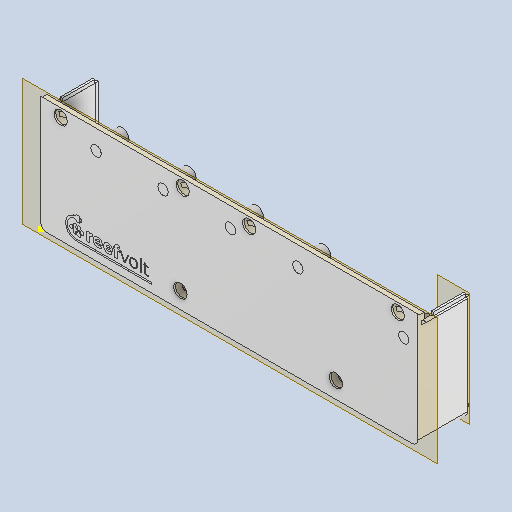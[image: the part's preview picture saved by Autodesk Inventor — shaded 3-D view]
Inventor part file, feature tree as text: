
AUTODESK INVENTOR PART (.ipt)
format: ipt  version: 2024.2 (Build 282272000, 272)  size: 966,656 bytes
history: native  units: in
note: dims shown in document units (in); Inventor stores cm internally (conversion verified against a paired STEP export)
features: reference x38, extrude x13, other x13, sketch x4, plane x3, chamfer x2, hole x1
ambient origin geometry x8: Origin, YZ Plane, XZ Plane, XY Plane, X Axis, Y Axis, Z Axis, Center Point
bodies: Solid1 (feature_tree)
feature tree (74):
  plane  "Work Plane1"
  plane  "Work Plane2"
  extrude  "Extrusion1"  Depth=0.1969in TaperAngle=0.0deg
  extrude  "Extrusion2"  Depth=0.0039in
  other  "Offset Top Of Cable Gland"
  other  "Offset from case bottom"
  extrude  "CableWall"  Depth=1.0in TaperAngle=0.0deg
  extrude  "CableInnerLid"  Depth=0.3937in TaperAngle=0.0deg
  extrude  "CableCutouts"  Depth=0.3937in
  extrude  "SideWallsToBottom"  Depth=0.3937in TaperAngle=0.0deg
  hole  "Hole1"  [1 undecoded]
  chamfer  "Chamfer1"  Distance=0.1575in
  extrude  "Extrusion8"  Depth=0.3937in
  extrude  "Extrusion9"  Depth=0.3937in
  plane  "Work Plane6"
  extrude  "LED Cutback"  Depth=0.3937in TaperAngle=0.0deg
  extrude  "LED Surface Boss"  Depth=0.3937in
  extrude  "Logo"  Depth=0.3937in
  extrude  "LED Tubes"  Depth=0.3937in TaperAngle=45.0deg
  extrude  "Extrusion14"  Depth=0.3937in
  chamfer  "Chamfer2"  Distance=0.0039in
  reference  "Reference2"
  sketch  "Sketch3"  dims[d0=0.125in d1=0.1969in d2=0.0in]
  reference  "Reference3"
  reference  "Reference4"
  reference  "Reference5"
  reference  "Reference6"
  reference  "Reference7"
  reference  "Reference8"
  reference  "Reference9"
  reference  "Reference10"
  reference  "Reference11"
  reference  "Reference12"
  reference  "Reference14"
  reference  "Reference15"
  sketch  "Sketch6"  dims[d3=0.0008in d4=0.0039in]
  reference  "Reference16"
  reference  "Reference17"
  reference  "Reference18"
  reference  "Reference19"
  reference  "Reference20"
  reference  "Reference23"
  reference  "Reference24"
  reference  "Reference25"
  reference  "Reference26"
  reference  "Reference27"
  reference  "Reference28"
  reference  "Reference29"
  reference  "Reference30"
  reference  "Reference31"
  reference  "Reference33"
  sketch  "Sketch13"  dims[d5=0.0039in d6=1.0in d7=0.0in]
  reference  "Reference34"
  reference  "Reference35"
  reference  "Reference36"
  reference  "Reference37"
  reference  "Reference38"
  sketch  "Sketch18"  dims[d8=0.1181in d9=1.0in d10=0.0in d11=0.1142in d12=0.0787in d13=0.0in d14=0.3937in d15=0.0in d16=0.1575in d17=0.0039in d18=0.0039in d21=0.3937in d22=0.0in d23=0.0039in d24=0.0079in d29=0.129in d30=0.75in d31=0.3in d32=0.1181in d33=0.5635in d34=1.0in d35=0.8108in d36=0.08in d37=0.125in d38=45.0deg d39=0.0039in d41=0.0039in d42=0.0in d43=0.0472in d44=0.0472in d45=0.0748in d46=0.0in d47=0.0039in d48=0.0748in d49=0.0in d50=0.1969in d51=-0.0157in d52=1.0in d53=0.0in d54=0.0004in d55=0.0in d56=0.0004in d57=0.0in d58=0.0394in d59=0.3937in d60=0.0in d61=0.0079in d62=0.0394in d63=0.0394in d64=0.0in d66=0.0394in d67=0.125in d68=45.0deg]
  reference  "Reference39"
  reference  "Reference40"
  reference  "Reference41"
  reference  "Reference42"
  reference  "Reference44"
  other  "<userpath>\Dropbox\elec\Mechanical\ReefVoltEssential\_TOP.iam"
  other  "_TOP.iam"
  other  "RV_ES_TopHV:1"
  other  "RV_ES_Bottom:1"
  other  "reefvolt_power_essentials_ESP32:2"
  other  "LED200_PLB"
  other  "LED200_PLC"
  other  "LED200_PLD"
  other  "LED200_PLA"
  other  "LED100"
  other  "reefvolt_power_essentials_ESP32_BOARD:1"
note: 1 required parameter value undecoded (feature->parameter linkage not recoverable at this tier; creation-order binding heuristic only, values carry confidence <= 0.55)
